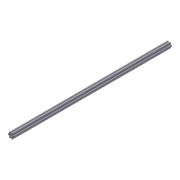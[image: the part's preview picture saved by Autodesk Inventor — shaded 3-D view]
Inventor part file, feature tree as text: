
AUTODESK INVENTOR PART (.ipt)
format: ipt  version: 2011 (Build 150239000, 239)  size: 116,736 bytes
history: native  units: in
note: dims shown in document units (in); Inventor stores cm internally (conversion verified against a paired STEP export)
features: other x3, extrude x1, sketch x1
ambient origin geometry x8: Origin, YZ Plane, XZ Plane, XY Plane, X Axis, Y Axis, Z Axis, Center Point
bodies: Solid1 (feature_tree)
feature tree (5):
  other  "Blocks"
  extrude  "Extrusion1"  [1 undecoded]
  sketch  "Sketch1"  dims[d0=14.875in d1=0.0in]
  other  "CrossHexProfile"
  other  "CrossHexProfile:1"
note: 1 required parameter value undecoded (feature->parameter linkage not recoverable at this tier; creation-order binding heuristic only, values carry confidence <= 0.55)
